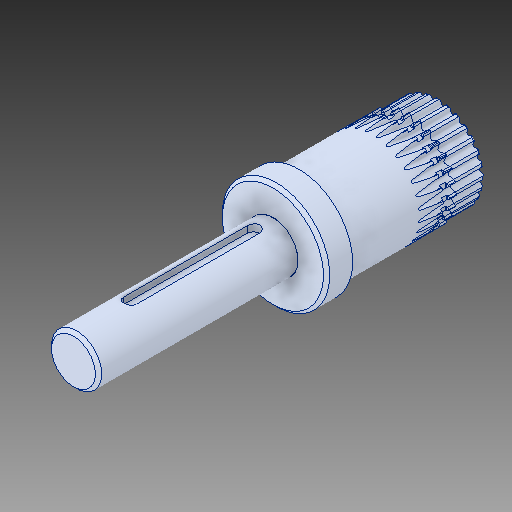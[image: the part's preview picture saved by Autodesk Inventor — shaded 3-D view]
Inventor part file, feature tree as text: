
AUTODESK INVENTOR PART (.ipt)
format: ipt  version: 2017 (Build 210142000, 142)  size: 1,452,032 bytes
history: native  units: in
note: dims shown in document units (in); Inventor stores cm internally (conversion verified against a paired STEP export)
features: other x1, chamfer x1
ambient origin geometry x8: Origin, YZ Plane, XZ Plane, XY Plane, X Axis, Y Axis, Z Axis, Center Point
bodies: Solid1 (feature_tree), Solid2 (feature_tree)
feature tree (2):
  other  "8MM CIM SHAFT"
  chamfer  "Chamfer3"  [1 undecoded]
note: 1 required parameter value undecoded (feature->parameter linkage not recoverable at this tier; creation-order binding heuristic only, values carry confidence <= 0.55)
